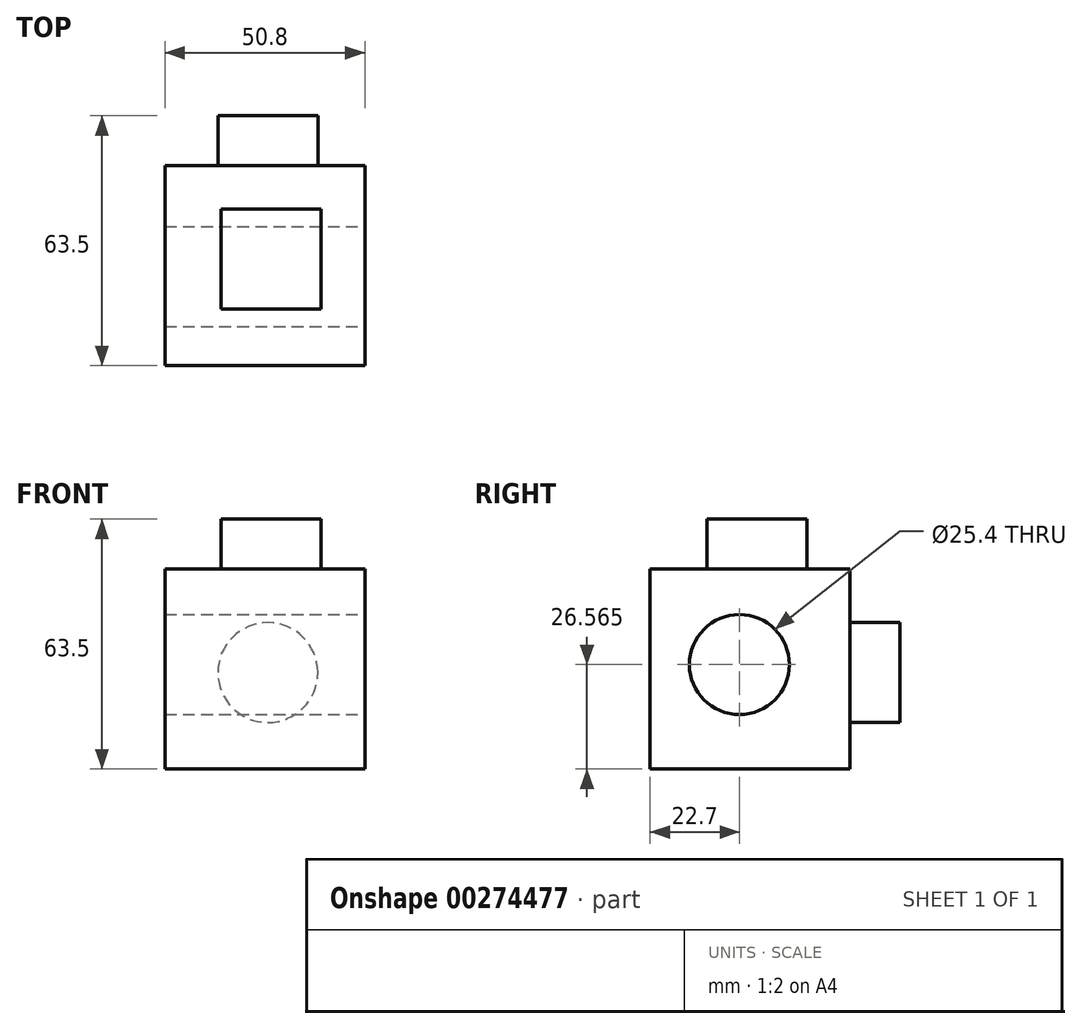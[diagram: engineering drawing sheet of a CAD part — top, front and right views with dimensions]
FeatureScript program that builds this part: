
annotation { "Feature Type Name" : "Feature", "Feature Type Description" : "" }
export const myFeature = defineFeature(function(context is Context, id is Id, definition is map)
    precondition{}
    {
        {
            var Q0;
            Q0=qCreatedBy(makeId("Top.planeOp"),FACE);
            var sketch = newSketch(context, id + "F0", { "sketchPlane" : qUnion([Q0])});
            skLineSegment(sketch, "E0.bottom", {"start": v(-55.19, 23.49) * mm, "end": v(-4.39, 23.49) * mm});
            skLineSegment(sketch, "E0.top", {"start": v(-55.19, 74.29) * mm, "end": v(-4.39, 74.29) * mm});
            skLineSegment(sketch, "E0.left", {"start": v(-55.19, 23.49) * mm, "end": v(-55.19, 74.29) * mm});
            skLineSegment(sketch, "E0.right", {"start": v(-4.39, 23.49) * mm, "end": v(-4.39, 74.29) * mm});
            skSolve(sketch);
        }
        {
            var Q0;
            Q0 = qSketchRegion(id + "F0", true);
            extrude(context, id + "F1", {"entities" : qUnion([Q0]), "depth" : 50.8 * mm});
        }
        {
            var Q0;
            Q0=makeQuery(id+"F1.opExtrude","SWEPT_FACE",FACE,{"disambiguationData":[OSD([sQuery(id+"F0.wireOp",EDGE,"E0.top")])]});
            var sketch = newSketch(context, id + "F2", { "sketchPlane" : qUnion([Q0])});
            skSolve(sketch);
        }
        {
            var Q0;
            {var subQ0=sQuery(id+"F0.wireOp",EDGE,"E0.top");Q0=makeQuery(id+"F2.imprint","IMPRINT",FACE,{"disambiguationData":[TD([[makeQuery(id+"F2.imprint","IMPRINT",EDGE,{"derivedFrom":makeQuery(id+"F1.opExtrude","CAP_EDGE",EDGE,{"disambiguationData":[OSD([subQ0])],"isStart":true})}),-1.0]])]});}
            var sketch = newSketch(context, id + "F3", { "sketchPlane" : qUnion([Q0])});
            skCircle(sketch, "E1", {"center": v(29.03, 24.52) * mm, "radius": 12.7 * mm});
            skSolve(sketch);
        }
        {
            var Q0;
            Q0 = qSketchRegion(id + "F3", true);
            extrude(context, id + "F4", {"entities" : qUnion([Q0]), "operationType" : NewBodyOperationType.ADD, "depth" : 12.7 * mm});
        }
        {
            var Q0;
            Q0=makeQuery(id+"F1.opExtrude","SWEPT_FACE",FACE,{"disambiguationData":[OSD([sQuery(id+"F0.wireOp",EDGE,"E0.right")])]});
            var sketch = newSketch(context, id + "F5", { "sketchPlane" : qUnion([Q0])});
            skCircle(sketch, "E2", {"center": v(46.2, 26.56) * mm, "radius": 12.7 * mm});
            skSolve(sketch);
        }
        {
            var Q0;
            Q0 = qSketchRegion(id + "F5", true);
            extrude(context, id + "F6", {"entities" : qUnion([Q0]), "operationType" : NewBodyOperationType.REMOVE, "oppositeDirection" : true, "depth" : 50.8 * mm});
        }
        {
            var Q0;
            Q0=makeQuery(id+"F1.opExtrude","CAP_FACE",FACE,{"disambiguationData":[OSD([sQuery(id+"F0.wireOp",EDGE,"E0.bottom"),sQuery(id+"F0.wireOp",EDGE,"E0.top"),sQuery(id+"F0.wireOp",EDGE,"E0.left"),sQuery(id+"F0.wireOp",EDGE,"E0.right")])],"isStart":false});
            var sketch = newSketch(context, id + "F7", { "sketchPlane" : qUnion([Q0])});
            skLineSegment(sketch, "E3", {"start": v(-40.9, 63.34) * mm, "end": v(-40.9, 37.94) * mm});
            skLineSegment(sketch, "E4", {"start": v(-40.9, 37.94) * mm, "end": v(-15.5, 37.94) * mm});
            skLineSegment(sketch, "E5", {"start": v(-15.5, 37.94) * mm, "end": v(-15.5, 63.34) * mm});
            skLineSegment(sketch, "E6", {"start": v(-15.5, 63.34) * mm, "end": v(-40.9, 63.34) * mm});
            skSolve(sketch);
        }
        {
            var Q0;
            Q0 = qSketchRegion(id + "F7", true);
            extrude(context, id + "F8", {"entities" : qUnion([Q0]), "operationType" : NewBodyOperationType.ADD, "depth" : 12.7 * mm});
        }
    });
